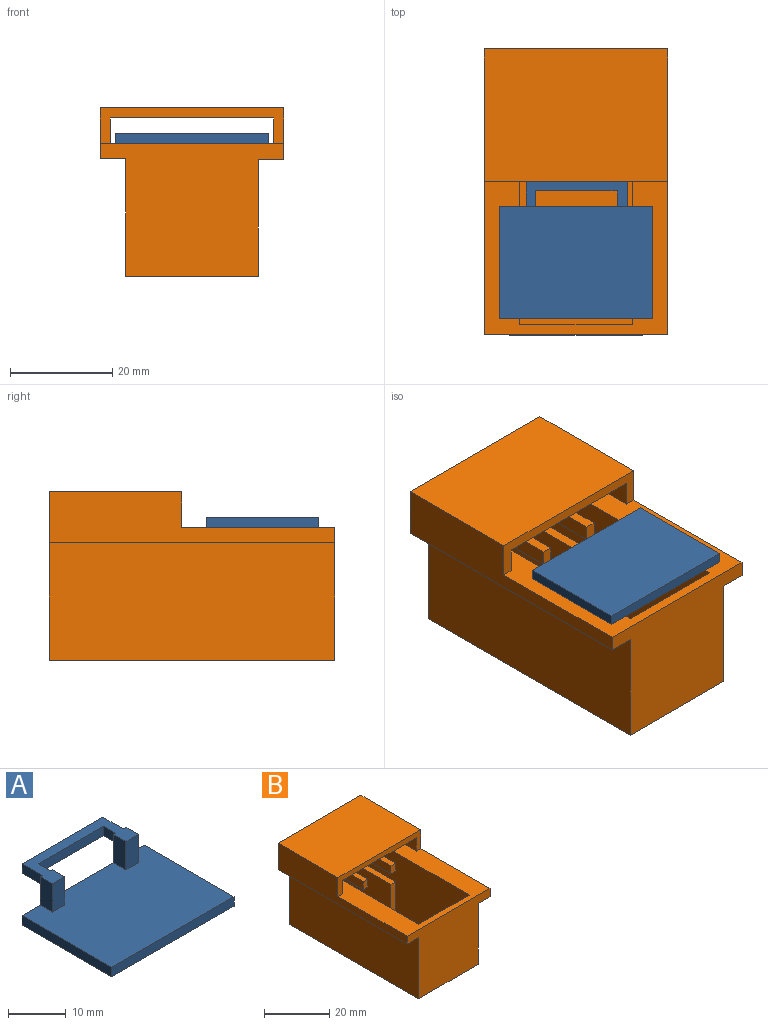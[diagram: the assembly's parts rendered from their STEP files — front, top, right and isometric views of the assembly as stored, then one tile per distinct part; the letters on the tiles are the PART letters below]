
ASSEMBLY  parts=2 mates=1
PART A: 20 faces, bbox 30x27x8 mm
  f0: plane 3x2mm, normal (-1,0,0), area 6mm2, adj f2,f11,f16,f19
  f1: plane 3x2mm, normal (1,0,0), area 6mm2, adj f2,f11,f16,f19
  f2: plane 30x8mm, normal (0,1,0), area 88.3mm2, adj f0,f1,f3,f4,f6,f7,f8,f10
  f3: plane 30x22mm, normal (0,0,1), area 642mm2, adj f2,f4,f5,f6,f8,f9,f10,f12
  f4: plane 22x2mm, normal (-1,0,0), area 44mm2, adj f2,f3,f5,f7
  f5: plane 30x2mm, normal (0,-1,0), area 60mm2, adj f3,f4,f6,f7
  f6: plane 22x2mm, normal (1,0,0), area 44mm2, adj f2,f3,f5,f7
  f7: plane 30x22mm, normal (0,0,-1), area 660mm2, adj f2,f4,f5,f6
  f8: plane 6x3mm, normal (-1,0,0), area 18mm2, adj f2,f3,f9,f11
  f9: plane 6x3mm, normal (0,-1,0), area 18mm2, adj f3,f8,f10,f11
  f10: plane 6x3mm, normal (1,0,0), area 18mm2, adj f2,f3,f9,f11
  f11: plane 21x8mm, normal (0,0,1), area 69.2mm2, adj f0,f1,f2,f8,f9,f10,f12,f13
  f12: plane 6x3mm, normal (0,-1,0), area 18mm2, adj f3,f11,f13,f14
  f13: plane 6x3mm, normal (1,0,0), area 18mm2, adj f2,f3,f11,f12
  f14: plane 6x3mm, normal (-1,0,0), area 18mm2, adj f2,f3,f11,f12
  f15: plane 5x2mm, normal (1,0,0), area 10mm2, adj f2,f11,f16,f17
  f16: plane 19.83x5mm, normal (0,0,-1), area 51.2mm2, adj f0,f1,f2,f15,f17,f18,f19
  f17: plane 19.83x2mm, normal (0,1,0), area 39.7mm2, adj f11,f15,f16,f18
  f18: plane 5x2mm, normal (-1,0,0), area 10mm2, adj f2,f11,f16,f17
  f19: plane 16x2mm, normal (0,-1,0), area 32mm2, adj f0,f1,f11,f16
PART B: 46 faces, bbox 36x56x33 mm
  f0: plane 3x2mm, normal (0,-1,0), area 6mm2, adj f9,f19,f25,f44
  f1: plane 4x2mm, normal (-1,0,0), area 8mm2, adj f6,f36,f37,f43
  f2: plane 24x17mm, normal (-1,0,0), area 408mm2, adj f18,f21,f26,f45
  f3: plane 17x2mm, normal (0,-1,0), area 34mm2, adj f18,f20,f23,f42
  f4: plane 24x3mm, normal (1,0,0), area 72mm2, adj f7,f9,f24,f40
  f5: plane 4x2mm, normal (1,0,0), area 8mm2, adj f6,f38,f39,f41
  f6: plane 36x33mm, normal (0,1,0), area 506.9mm2, adj f1,f5,f9,f11,f13,f14,f15,f17
  f7: plane 4x3mm, normal (0,-1,0), area 12mm2, adj f4,f9,f17,f38
  f8: plane 4x3mm, normal (0,-1,0), area 12mm2, adj f9,f15,f25,f36
  f9: plane 56x36mm, normal (0,0,1), area 844mm2, adj f0,f4,f6,f7,f8,f12,f15,f16
  f10: plane 10x2mm, normal (0,1,0), area 20mm2, adj f14,f18,f19,f20
  f11: plane 56x23mm, normal (-1,0,0), area 1288mm2, adj f6,f12,f14,f27
  f12: plane 36x26mm, normal (0,-1,0), area 706.9mm2, adj f9,f11,f13,f14,f27,f28,f29,f30
  f13: plane 56x22.83mm, normal (1,0,0), area 1278.3mm2, adj f6,f12,f14,f29
  f14: plane 56x26mm, normal (0,0,-1), area 1196mm2, adj f6,f10,f11,f12,f13,f19,f20
  f15: plane 54x24mm, normal (1,0,0), area 1256mm2, adj f6,f8,f9,f16,f18,f26,f36,f37
  f16: plane 24x22mm, normal (0,1,0), area 528mm2, adj f9,f15,f17,f18
  f17: plane 54x24mm, normal (-1,0,0), area 1256mm2, adj f6,f7,f9,f16,f18,f22,f38,f39
  f18: plane 52x22mm, normal (0,0,1), area 808mm2, adj f2,f3,f10,f15,f16,f17,f21,f22
  f19: plane 26x26mm, normal (1,0,0), area 580mm2, adj f0,f6,f9,f10,f14,f21,f43,f44
  f20: plane 26x26mm, normal (-1,0,0), area 580mm2, adj f3,f6,f9,f10,f14,f24,f40,f41
  f21: plane 17x2mm, normal (0,-1,0), area 34mm2, adj f2,f18,f19,f45
  f22: plane 17x4mm, normal (0,-1,0), area 68mm2, adj f17,f18,f23,f39
  f23: plane 24x17mm, normal (1,0,0), area 408mm2, adj f3,f18,f22,f42
  f24: plane 3x2mm, normal (0,-1,0), area 6mm2, adj f4,f9,f20,f40
  f25: plane 24x3mm, normal (-1,0,0), area 72mm2, adj f0,f8,f9,f44
  f26: plane 17x4mm, normal (0,-1,0), area 68mm2, adj f2,f15,f18,f37
  f27: plane 56x5mm, normal (0,0,-1), area 280mm2, adj f6,f11,f12,f28
  f28: plane 56x10mm, normal (-1,0,0), area 350mm2, adj f6,f9,f12,f27,f31,f35
  f29: plane 56x5mm, normal (0,0,-1), area 280mm2, adj f6,f12,f13,f30
  f30: plane 56x10.17mm, normal (1,0,0), area 359.7mm2, adj f6,f9,f12,f29,f31,f35
  f31: plane 36x7mm, normal (0,-1,0), area 92mm2, adj f9,f28,f30,f32,f33,f34,f35
  f32: plane 26x5mm, normal (1,0,0), area 130mm2, adj f6,f9,f31,f34
  f33: plane 26x5mm, normal (-1,0,0), area 130mm2, adj f6,f9,f31,f34
  f34: plane 32x26mm, normal (0,0,-1), area 832mm2, adj f6,f31,f32,f33
  f35: plane 36x26mm, normal (0,0,1), area 936mm2, adj f6,f28,f30,f31
  f36: plane 4x2mm, normal (0,0,-1), area 8mm2, adj f1,f6,f8,f15
  f37: plane 4x2mm, normal (0,0,1), area 8mm2, adj f1,f6,f15,f26
  f38: plane 4x2mm, normal (0,0,-1), area 8mm2, adj f5,f6,f7,f17
  f39: plane 4x2mm, normal (0,0,1), area 8mm2, adj f5,f6,f17,f22
  f40: plane 24x2mm, normal (0,0,-1), area 48mm2, adj f4,f20,f24,f41
  f41: plane 4x2mm, normal (0,-1,0), area 8mm2, adj f5,f20,f40,f42
  f42: plane 24x2mm, normal (0,0,1), area 48mm2, adj f3,f20,f23,f41
  f43: plane 4x2mm, normal (0,-1,0), area 8mm2, adj f1,f19,f44,f45
  f44: plane 24x2mm, normal (0,0,-1), area 48mm2, adj f0,f19,f25,f43
  f45: plane 24x2mm, normal (0,0,1), area 48mm2, adj f2,f19,f21,f43
PLACE A rot(axis=(0,1,0),180deg) t=(-30.48,-3,28)mm
PLACE B at identity fixed
MATE planar A.f3 <-> B.f9  axis (0,0,-1) through (13.04,13.93,26)mm
